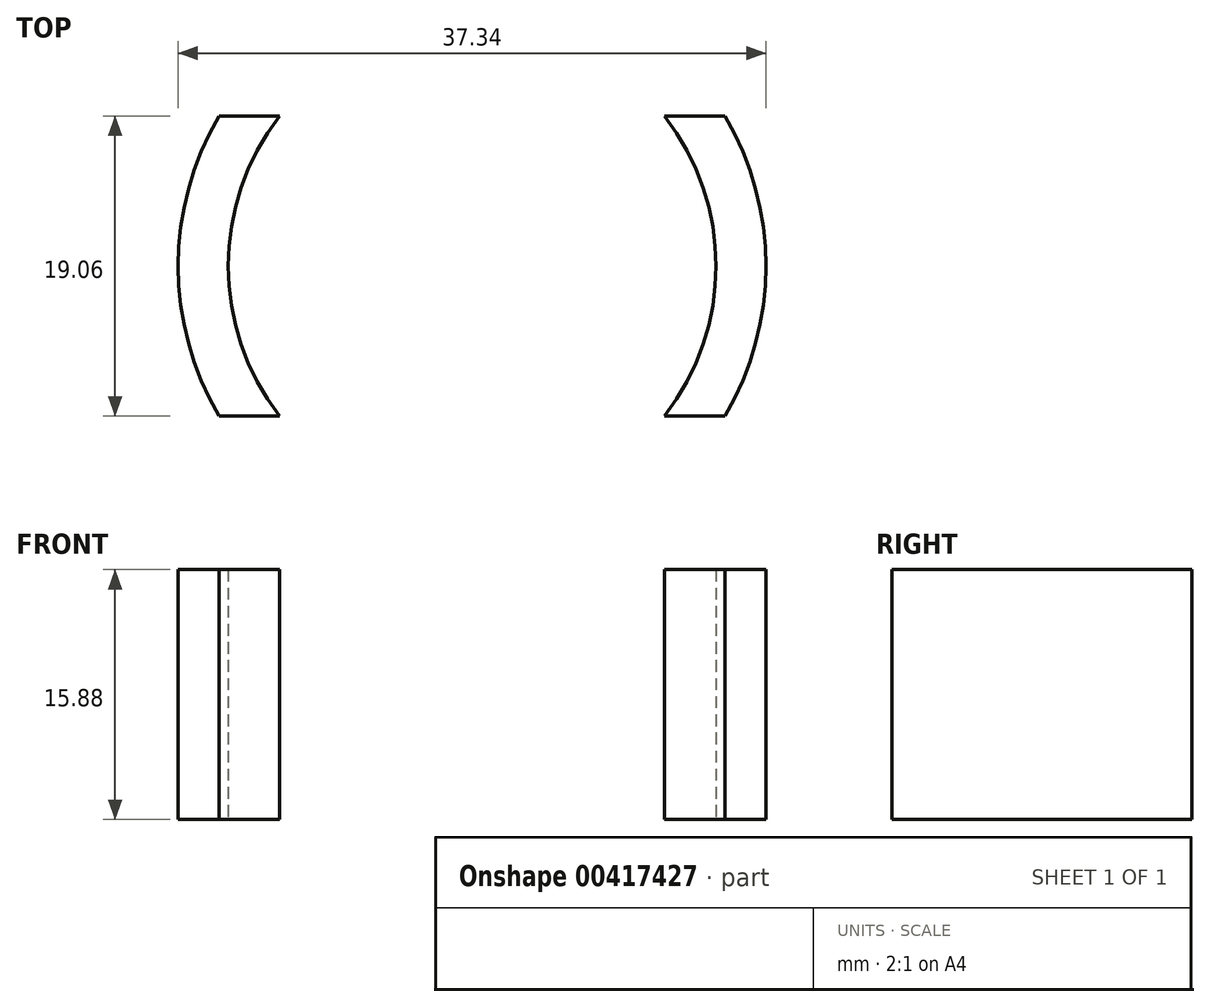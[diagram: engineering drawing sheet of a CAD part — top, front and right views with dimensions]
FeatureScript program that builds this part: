
annotation { "Feature Type Name" : "Feature", "Feature Type Description" : "" }
export const myFeature = defineFeature(function(context is Context, id is Id, definition is map)
    precondition{}
    {
        {
            var Q0;
            Q0=qCreatedBy(makeId("Top.planeOp"),FACE);
            var sketch = newSketch(context, id + "F0", { "sketchPlane" : qUnion([Q0])});
            skArc(sketch, "E0", {"start": v(-12.22, 9.52) * mm, "mid": v(-15.5, 0) * mm, "end": v(-12.22, -9.52) * mm});
            skArc(sketch, "E1", {"start": v(-16.06, 9.53) * mm, "mid": v(-18.67, 0) * mm, "end": v(-16.06, -9.53) * mm});
            skLineSegment(sketch, "E2", {"start": v(-16.06, 9.53) * mm, "end": v(16.06, 9.53) * mm});
            skLineSegment(sketch, "E3", {"start": v(-16.06, -9.52) * mm, "end": v(16.06, -9.52) * mm});
            skArc(sketch, "E4.trimOffspring", {"start": v(16.06, -9.53) * mm, "mid": v(18.67, 0) * mm, "end": v(16.06, 9.53) * mm});
            skArc(sketch, "E5.trimOffspring", {"start": v(12.22, -9.53) * mm, "mid": v(15.5, 0) * mm, "end": v(12.22, 9.52) * mm});
            skSolve(sketch);
        }
        {
            var Q0;
            {var subQ0=sQuery(id+"F0.wireOp",EDGE,"E0");Q0=makeQuery(id+"F0.imprint","IMPRINT",FACE,{"disambiguationData":[TD([[makeQuery(id+"F0.imprint","IMPRINT",EDGE,{"derivedFrom":subQ0}),-1.0]])]});}
            var Q1;
            {var subQ0=sQuery(id+"F0.wireOp",EDGE,"E4.trimOffspring");Q1=makeQuery(id+"F0.imprint","IMPRINT",FACE,{"disambiguationData":[TD([[makeQuery(id+"F0.imprint","IMPRINT",EDGE,{"derivedFrom":subQ0}),1.0]])]});}
            extrude(context, id + "F1", {"entities" : qUnion([Q0, Q1]), "depth" : 15.88 * mm, "offsetDistance" : 25.4 * mm});
        }
    });
